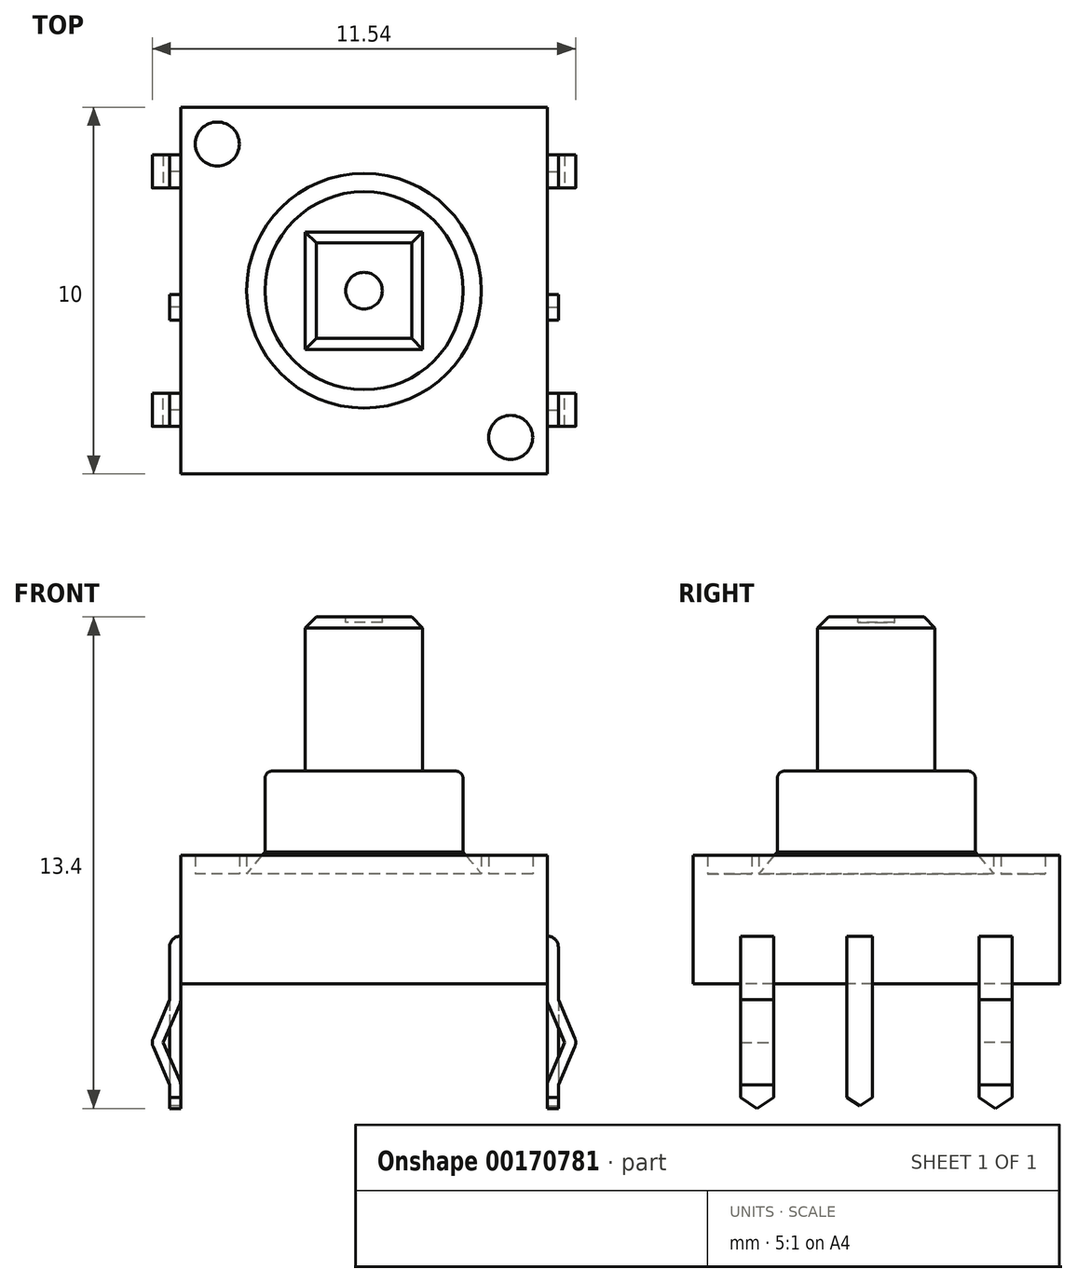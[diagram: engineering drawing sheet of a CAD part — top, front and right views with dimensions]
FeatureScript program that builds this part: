
annotation { "Feature Type Name" : "Feature", "Feature Type Description" : "" }
export const myFeature = defineFeature(function(context is Context, id is Id, definition is map)
    precondition{}
    {
        {
            var Q0;
            Q0=qCreatedBy(makeId("Top.planeOp"),FACE);
            var sketch = newSketch(context, id + "F0", { "sketchPlane" : qUnion([Q0])});
            skLineSegment(sketch, "E0.bottom", {"start": v(-5, 5) * mm, "end": v(5, 5) * mm});
            skLineSegment(sketch, "E0.top", {"start": v(-5, -5) * mm, "end": v(5, -5) * mm});
            skLineSegment(sketch, "E0.left", {"start": v(-5, 5) * mm, "end": v(-5, -5) * mm});
            skLineSegment(sketch, "E0.right", {"start": v(5, 5) * mm, "end": v(5, -5) * mm});
            skLineSegment(sketch, "E1", {"start": v(5, 5) * mm, "end": v(-5, -5) * mm, "construction": true});
            skSolve(sketch);
        }
        {
            var Q0;
            Q0 = qSketchRegion(id + "F0", true);
            extrude(context, id + "F1", {"entities" : qUnion([Q0]), "depth" : 3 * mm, "offsetDistance" : 25 * mm});
        }
        {
            var Q0;
            Q0=makeQuery(id+"F1.opExtrude","CAP_FACE",FACE,{"disambiguationData":[OSD([sQuery(id+"F0.wireOp",EDGE,"E0.bottom"),sQuery(id+"F0.wireOp",EDGE,"E0.top"),sQuery(id+"F0.wireOp",EDGE,"E0.left"),sQuery(id+"F0.wireOp",EDGE,"E0.right")])],"isStart":false});
            var sketch = newSketch(context, id + "F2", { "sketchPlane" : qUnion([Q0])});
            skLineSegment(sketch, "E2.0", {"start": v(-5, 5) * mm, "end": v(-5, -5) * mm});
            skLineSegment(sketch, "E2.1", {"start": v(-5, 5) * mm, "end": v(5, 5) * mm});
            skLineSegment(sketch, "E2.2", {"start": v(5, 5) * mm, "end": v(5, -5) * mm});
            skLineSegment(sketch, "E2.3", {"start": v(-5, -5) * mm, "end": v(5, -5) * mm});
            skCircle(sketch, "E3", {"center": v(4, 4) * mm, "radius": 0.6 * mm});
            skCircle(sketch, "E4.MirrorC", {"center": v(-4, 4) * mm, "radius": 0.6 * mm});
            skCircle(sketch, "E5.MirrorC", {"center": v(-4, -4) * mm, "radius": 0.6 * mm});
            skCircle(sketch, "E6.MirrorC", {"center": v(4, -4) * mm, "radius": 0.6 * mm});
            skCircle(sketch, "E7", {"center": v(0, 0) * mm, "radius": 3.2 * mm});
            skLineSegment(sketch, "E8", {"start": v(4, 5) * mm, "end": v(4, 4) * mm, "construction": true});
            skLineSegment(sketch, "E9", {"start": v(5, 4) * mm, "end": v(4, 4) * mm, "construction": true});
            skSolve(sketch);
        }
        {
            var Q0;
            Q0 = qSketchRegion(id + "F2", true);
            extrude(context, id + "F3", {"entities" : qUnion([Q0]), "depth" : 0.15 * mm, "offsetDistance" : 25 * mm});
        }
        {
            var Q0;
            Q0=makeQuery(id+"F2.imprint","IMPRINT",FACE,{"disambiguationData":[TD([[makeQuery(id+"F2.imprint","IMPRINT",EDGE,{"derivedFrom":sQuery(id+"F2.wireOp",EDGE,"E4.MirrorC")}),-1.0]])]});
            var Q1;
            Q1=makeQuery(id+"F2.imprint","IMPRINT",FACE,{"disambiguationData":[TD([[makeQuery(id+"F2.imprint","IMPRINT",EDGE,{"derivedFrom":sQuery(id+"F2.wireOp",EDGE,"E6.MirrorC")}),-1.0]])]});
            var Q2;
            Q2=makeQuery(id+"F2.imprint","IMPRINT",FACE,{"disambiguationData":[TD([[makeQuery(id+"F2.imprint","IMPRINT",EDGE,{"derivedFrom":sQuery(id+"F2.wireOp",EDGE,"E3")}),1.0]])]});
            var Q3;
            Q3=makeQuery(id+"F2.imprint","IMPRINT",FACE,{"disambiguationData":[TD([[makeQuery(id+"F2.imprint","IMPRINT",EDGE,{"derivedFrom":sQuery(id+"F2.wireOp",EDGE,"E5.MirrorC")}),1.0]])]});
            extrude(context, id + "F4", {"entities" : qUnion([Q0, Q1, Q2, Q3]), "operationType" : NewBodyOperationType.ADD, "depth" : 0.5 * mm, "offsetDistance" : 25 * mm});
        }
        {
            var Q0;
            Q0=qCreatedBy(makeId("Front.planeOp"),FACE);
            var sketch = newSketch(context, id + "F5", { "sketchPlane" : qUnion([Q0])});
            skLineSegment(sketch, "E10", {"start": v(0, 3) * mm, "end": v(-3.2, 3) * mm});
            skLineSegment(sketch, "E11", {"start": v(-3.2, 3) * mm, "end": v(-2.7, 3.6) * mm});
            skLineSegment(sketch, "E12", {"start": v(-2.7, 3.6) * mm, "end": v(0, 3.6) * mm});
            skLineSegment(sketch, "E13", {"start": v(0, 3.6) * mm, "end": v(0, 3) * mm});
            skLineSegment(sketch, "E14", {"start": v(-2.7, 3.6) * mm, "end": v(-2.7, 5.8) * mm});
            skLineSegment(sketch, "E15", {"start": v(-2.7, 5.8) * mm, "end": v(0, 5.8) * mm});
            skLineSegment(sketch, "E16", {"start": v(0, 5.8) * mm, "end": v(0, 3.6) * mm});
            skLineSegment(sketch, "E17.0", {"start": v(-3.2, 3) * mm, "end": v(3.2, 3) * mm, "construction": true});
            skSolve(sketch);
        }
        {
            var Q0;
            Q0 = qSketchRegion(id + "F5", true);
            var Q1;
            Q1=sQuery(id+"F5.wireOp",EDGE,"E16");
            revolve(context, id + "F6", {"operationType" : NewBodyOperationType.ADD, "surfaceOperationType" : NewSurfaceOperationType.NEW, "entities" : qUnion([Q0]), "axis" : qUnion([Q1]), "revolveType" : RevolveType.FULL});
        }
        {
            var Q0;
            Q0=makeQuery(id+"F6.opRevolve","SWEPT_FACE",FACE,{"disambiguationData":[OSD([sQuery(id+"F5.wireOp",EDGE,"E15")])]});
            var sketch = newSketch(context, id + "F7", { "sketchPlane" : qUnion([Q0])});
            skLineSegment(sketch, "E18.bottom", {"start": v(1.6, 1.6) * mm, "end": v(-1.6, 1.6) * mm});
            skLineSegment(sketch, "E18.top", {"start": v(1.6, -1.6) * mm, "end": v(-1.6, -1.6) * mm});
            skLineSegment(sketch, "E18.left", {"start": v(1.6, 1.6) * mm, "end": v(1.6, -1.6) * mm});
            skLineSegment(sketch, "E18.right", {"start": v(-1.6, 1.6) * mm, "end": v(-1.6, -1.6) * mm});
            skLineSegment(sketch, "E19", {"start": v(-1.6, 1.6) * mm, "end": v(1.6, -1.6) * mm, "construction": true});
            skSolve(sketch);
        }
        {
            var Q0;
            Q0 = qSketchRegion(id + "F7", true);
            extrude(context, id + "F8", {"entities" : qUnion([Q0]), "operationType" : NewBodyOperationType.ADD, "depth" : (10 - 5.8) * mm, "offsetDistance" : 25 * mm});
        }
        {
            var Q0;
            Q0=makeQuery(id+"F8.opExtrude","CAP_FACE",FACE,{"disambiguationData":[OSD([sQuery(id+"F7.wireOp",EDGE,"E18.bottom"),sQuery(id+"F7.wireOp",EDGE,"E18.top"),sQuery(id+"F7.wireOp",EDGE,"E18.left"),sQuery(id+"F7.wireOp",EDGE,"E18.right")])],"isStart":false});
            var sketch = newSketch(context, id + "F9", { "sketchPlane" : qUnion([Q0])});
            skCircle(sketch, "E20", {"center": v(0, 0) * mm, "radius": 0.5 * mm});
            skSolve(sketch);
        }
        {
            var Q0;
            Q0 = qSketchRegion(id + "F9", true);
            extrude(context, id + "F10", {"entities" : qUnion([Q0]), "operationType" : NewBodyOperationType.REMOVE, "oppositeDirection" : true, "depth" : 0.15 * mm, "offsetDistance" : 25 * mm});
        }
        {
            var Q0;
            Q0=makeQuery(id+"F8.opExtrude","CAP_EDGE",EDGE,{"disambiguationData":[OSD([sQuery(id+"F7.wireOp",EDGE,"E18.right")])],"isStart":false});
            var Q1;
            Q1=makeQuery(id+"F8.opExtrude","CAP_EDGE",EDGE,{"disambiguationData":[OSD([sQuery(id+"F7.wireOp",EDGE,"E18.top")])],"isStart":false});
            var Q2;
            Q2=makeQuery(id+"F8.opExtrude","CAP_EDGE",EDGE,{"disambiguationData":[OSD([sQuery(id+"F7.wireOp",EDGE,"E18.left")])],"isStart":false});
            var Q3;
            Q3=makeQuery(id+"F8.opExtrude","CAP_EDGE",EDGE,{"disambiguationData":[OSD([sQuery(id+"F7.wireOp",EDGE,"E18.bottom")])],"isStart":false});
            chamfer(context, id + "F11", {"entities" : qUnion([Q0, Q1, Q2, Q3]), "width" : 0.3 * mm, "tangentPropagation" : true});
        }
        {
            var Q0;
            Q0=makeQuery(id+"F6.opRevolve","SWEPT_EDGE",EDGE,{"disambiguationData":[OSD([sQuery(id+"F5.wireOp",EDGE,"E14"),sQuery(id+"F5.wireOp",EDGE,"E15")])]});
            fillet(context, id + "F12", {"entities" : qUnion([Q0]), "radius" : 0.2 * mm, "tangentPropagation" : true, "allowEdgeOverflow" : false});
        }
        {
            var Q0;
            Q0=qCreatedBy(makeId("Front.planeOp"),FACE);
            cPlane(context, id + "F13", {"entities" : qUnion([Q0]), "cplaneType" : CPlaneType.OFFSET, "offset" : (6.5 / 2) * mm, "width" : 150 * mm, "height" : 150 * mm});
        }
        {
            var Q0;
            Q0=qCreatedBy(id+"F13.planeOp",FACE);
            var sketch = newSketch(context, id + "F14", { "sketchPlane" : qUnion([Q0])});
            skLineSegment(sketch, "E21", {"start": v(-5, 1.3) * mm, "end": v(-5, -0.5) * mm});
            skLineSegment(sketch, "E22", {"start": v(-5, -0.5) * mm, "end": v(-5.47, -1.6) * mm});
            skLineSegment(sketch, "E23", {"start": v(-5.47, -1.6) * mm, "end": v(-5, -2.7) * mm});
            skLineSegment(sketch, "E24", {"start": v(-5, -2.7) * mm, "end": v(-5, -3.5) * mm});
            skLineSegment(sketch, "E25", {"start": v(-5, -3.5) * mm, "end": v(-5.3, -3.5) * mm});
            skLineSegment(sketch, "E26", {"start": v(-5.3, -3.5) * mm, "end": v(-5.3, -2.76) * mm});
            skLineSegment(sketch, "E27", {"start": v(-5.3, -2.76) * mm, "end": v(-5.8, -1.6) * mm});
            skLineSegment(sketch, "E28", {"start": v(-5.8, -1.6) * mm, "end": v(-5.3, -0.44) * mm});
            skLineSegment(sketch, "E29", {"start": v(-5.3, -0.44) * mm, "end": v(-5.3, 1.3) * mm});
            skLineSegment(sketch, "E30", {"start": v(-5.3, 1.3) * mm, "end": v(-5, 1.3) * mm});
            skLineSegment(sketch, "E31", {"start": v(-5.47, -1.6) * mm, "end": v(-5.75, -1.48) * mm, "construction": true});
            skLineSegment(sketch, "E32", {"start": v(-5.47, -1.6) * mm, "end": v(-5.75, -1.72) * mm, "construction": true});
            skSolve(sketch);
        }
        {
            var Q0;
            Q0 = qSketchRegion(id + "F14", true);
            extrude(context, id + "F15", {"entities" : qUnion([Q0]), "depth" : 0.9 * mm, "offsetDistance" : 25 * mm, "symmetric" : true});
        }
        {
            var Q0;
            Q0=qCreatedBy(makeId("Front.planeOp"),FACE);
            cPlane(context, id + "F16", {"entities" : qUnion([Q0]), "cplaneType" : CPlaneType.OFFSET, "offset" : 0.45 * mm, "width" : 150 * mm, "height" : 150 * mm});
        }
        {
            var Q0;
            Q0=qCreatedBy(id+"F16.planeOp",FACE);
            var sketch = newSketch(context, id + "F17", { "sketchPlane" : qUnion([Q0])});
            skLineSegment(sketch, "E33.bottom", {"start": v(-5, 1.3) * mm, "end": v(-5.3, 1.3) * mm});
            skLineSegment(sketch, "E33.top", {"start": v(-5, -3.5) * mm, "end": v(-5.3, -3.5) * mm});
            skLineSegment(sketch, "E33.left", {"start": v(-5, 1.3) * mm, "end": v(-5, -3.5) * mm});
            skLineSegment(sketch, "E33.right", {"start": v(-5.3, 1.3) * mm, "end": v(-5.3, -3.5) * mm});
            skSolve(sketch);
        }
        {
            var Q0;
            Q0 = qSketchRegion(id + "F17", true);
            extrude(context, id + "F18", {"entities" : qUnion([Q0]), "depth" : 0.7 * mm, "offsetDistance" : 25 * mm, "symmetric" : true});
        }
        {
            var Q0;
            Q0=makeQuery(id+"F15.opExtrude","CAP_EDGE",EDGE,{"disambiguationData":[OSD([sQuery(id+"F14.wireOp",EDGE,"E25")])],"isStart":false});
            var Q1;
            Q1=makeQuery(id+"F15.opExtrude","CAP_EDGE",EDGE,{"disambiguationData":[OSD([sQuery(id+"F14.wireOp",EDGE,"E25")])],"isStart":true});
            var Q2;
            Q2=makeQuery(id+"F18.opExtrude","CAP_EDGE",EDGE,{"disambiguationData":[OSD([sQuery(id+"F17.wireOp",EDGE,"E33.top")])],"isStart":false});
            var Q3;
            Q3=makeQuery(id+"F18.opExtrude","CAP_EDGE",EDGE,{"disambiguationData":[OSD([sQuery(id+"F17.wireOp",EDGE,"E33.top")])],"isStart":true});
            chamfer(context, id + "F19", {"entities" : qUnion([Q0, Q1, Q2, Q3]), "chamferType" : ChamferType.TWO_OFFSETS, "width1" : 0.4 * mm, "oppositeDirection" : false, "width2" : 0.6 * mm, "tangentPropagation" : true});
        }
        {
            var Q0;
            Q0=makeQuery(id+"F15.opExtrude","SWEPT_EDGE",EDGE,{"disambiguationData":[OSD([sQuery(id+"F14.wireOp",EDGE,"E27"),sQuery(id+"F14.wireOp",EDGE,"E28")])]});
            var Q1;
            Q1=makeQuery(id+"F15.opExtrude","SWEPT_EDGE",EDGE,{"disambiguationData":[OSD([sQuery(id+"F14.wireOp",EDGE,"E29"),sQuery(id+"F14.wireOp",EDGE,"E30")])]});
            var Q2;
            Q2=makeQuery(id+"F15.opExtrude","SWEPT_EDGE",EDGE,{"disambiguationData":[OSD([sQuery(id+"F14.wireOp",EDGE,"E23"),sQuery(id+"F14.wireOp",EDGE,"E24")])]});
            var Q3;
            Q3=makeQuery(id+"F15.opExtrude","SWEPT_EDGE",EDGE,{"disambiguationData":[OSD([sQuery(id+"F14.wireOp",EDGE,"E21"),sQuery(id+"F14.wireOp",EDGE,"E22")])]});
            var Q4;
            Q4=makeQuery(id+"F18.opExtrude","SWEPT_EDGE",EDGE,{"disambiguationData":[OSD([sQuery(id+"F17.wireOp",EDGE,"E33.bottom"),sQuery(id+"F17.wireOp",EDGE,"E33.right")])]});
            fillet(context, id + "F20", {"entities" : qUnion([Q0, Q1, Q2, Q3, Q4]), "radius" : 0.3 * mm, "tangentPropagation" : true, "allowEdgeOverflow" : false});
        }
        {
            var Q0;
            Q0=makeQuery(id+"F15.opExtrude","SWEPT_BODY",BODY,{"disambiguationData":[OSD([sQuery(id+"F14.wireOp",EDGE,"E21"),sQuery(id+"F14.wireOp",EDGE,"E22"),sQuery(id+"F14.wireOp",EDGE,"E23"),sQuery(id+"F14.wireOp",EDGE,"E24"),sQuery(id+"F14.wireOp",EDGE,"E25"),sQuery(id+"F14.wireOp",EDGE,"E26"),sQuery(id+"F14.wireOp",EDGE,"E27"),sQuery(id+"F14.wireOp",EDGE,"E28"),sQuery(id+"F14.wireOp",EDGE,"E29"),sQuery(id+"F14.wireOp",EDGE,"E30")])]});
            var Q1;
            Q1=qCreatedBy(makeId("Front.planeOp"),FACE);
            mirror(context, id + "F21", {"entities" : qUnion([Q0]), "mirrorPlane" : qUnion([Q1])});
        }
        {
            var Q0;
            Q0=makeQuery(id+"F21.opPattern","COPY",BODY,{"derivedFrom":makeQuery(id+"F15.opExtrude","SWEPT_BODY",BODY,{"disambiguationData":[OSD([sQuery(id+"F14.wireOp",EDGE,"E21"),sQuery(id+"F14.wireOp",EDGE,"E22"),sQuery(id+"F14.wireOp",EDGE,"E23"),sQuery(id+"F14.wireOp",EDGE,"E24"),sQuery(id+"F14.wireOp",EDGE,"E25"),sQuery(id+"F14.wireOp",EDGE,"E26"),sQuery(id+"F14.wireOp",EDGE,"E27"),sQuery(id+"F14.wireOp",EDGE,"E28"),sQuery(id+"F14.wireOp",EDGE,"E29"),sQuery(id+"F14.wireOp",EDGE,"E30")])]}),"instanceName":"1"});
            var Q1;
            Q1=makeQuery(id+"F15.opExtrude","SWEPT_BODY",BODY,{"disambiguationData":[OSD([sQuery(id+"F14.wireOp",EDGE,"E21"),sQuery(id+"F14.wireOp",EDGE,"E22"),sQuery(id+"F14.wireOp",EDGE,"E23"),sQuery(id+"F14.wireOp",EDGE,"E24"),sQuery(id+"F14.wireOp",EDGE,"E25"),sQuery(id+"F14.wireOp",EDGE,"E26"),sQuery(id+"F14.wireOp",EDGE,"E27"),sQuery(id+"F14.wireOp",EDGE,"E28"),sQuery(id+"F14.wireOp",EDGE,"E29"),sQuery(id+"F14.wireOp",EDGE,"E30")])]});
            var Q2;
            Q2=makeQuery(id+"F18.opExtrude","SWEPT_BODY",BODY,{"disambiguationData":[OSD([sQuery(id+"F17.wireOp",EDGE,"E33.bottom"),sQuery(id+"F17.wireOp",EDGE,"E33.top"),sQuery(id+"F17.wireOp",EDGE,"E33.left"),sQuery(id+"F17.wireOp",EDGE,"E33.right")])]});
            var Q3;
            Q3=qCreatedBy(makeId("Right.planeOp"),FACE);
            mirror(context, id + "F22", {"entities" : qUnion([Q0, Q1, Q2]), "mirrorPlane" : qUnion([Q3])});
        }
    });
